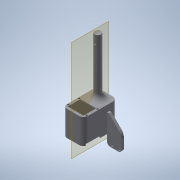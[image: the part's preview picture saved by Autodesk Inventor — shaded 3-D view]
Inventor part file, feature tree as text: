
AUTODESK INVENTOR PART (.ipt)
format: ipt  version: 2020.1 (Build 241239000, 239)  size: 274,432 bytes
history: native  units: mm
features: extrude x10, sketch x9, fillet x4, chamfer x1, plane x1, mirror x1
ambient origin geometry x8: Origin, YZ Plane, XZ Plane, XY Plane, X Axis, Y Axis, Z Axis, Center Point
bodies: Solid1 (feature_tree)
feature tree (26):
  sketch  "Sketch1"  dims[d0=25.0mm d1=45.5mm]
  extrude  "Extrusion1"  Depth=45.5mm
  extrude  "Extrusion2"  Depth=40.0mm TaperAngle=0.0deg
  extrude  "Extrusion3"  Depth=3.0mm
  extrude  "Extrusion4"  Depth=38.0mm TaperAngle=0.0deg
  fillet  "Fillet1"  Radius=10.3mm
  extrude  "Extrusion5"  Depth=90.0mm TaperAngle=0.0deg
  fillet  "Fillet2"  Radius=10.0mm
  extrude  "Extrusion6"  Depth=3.0mm
  extrude  "Extrusion7"  Depth=7.0mm
  chamfer  "Chamfer1"  Distance=3.0mm
  extrude  "Extrusion8"  Depth=3.0mm
  fillet  "Fillet3"  Radius=2.8mm
  extrude  "Extrusion9"  Depth=10.0mm
  fillet  "Fillet4"  Radius=2.8mm
  plane  "Work Plane1"
  mirror  "Mirror1"
  extrude  "Extrusion10"  Depth=10.0mm
  sketch  "Sketch2"  dims[d2=4.0mm d3=40.0mm d4=0.0mm]
  sketch  "Sketch3"  dims[d5=38.0mm d6=0.0mm d7=3.0mm]
  sketch  "Sketch4"  dims[d8=23.0mm d9=38.0mm d10=0.0mm d11=10.3mm]
  sketch  "Sketch5"  dims[d12=10.0mm d13=90.0mm d14=0.0mm d15=10.0mm]
  sketch  "Sketch6"  dims[d16=13.0mm d17=3.0mm]
  sketch  "Sketch7"  dims[d18=90.0mm d19=0.0mm d20=7.0mm]
  sketch  "Sketch8"  dims[d21=3.0mm]
  sketch  "Sketch9"  dims[d22=3.0mm d23=3.0mm d24=3.0mm d25=2.8mm d26=2.8mm d27=2.8mm d28=2.8mm d29=90.0mm d30=0.0mm d31=2.0mm d32=30.0mm d33=4.0mm d34=23.0mm d35=0.0mm d36=20.0mm d37=2.0mm d38=45.0deg d39=15.0mm d40=0.0mm d41=5.0mm d42=3.0mm d43=8.0mm d44=4.0mm d45=3.0mm d46=3.0mm d47=15.0mm d48=0.0mm d49=15.0mm d50=12.5mm d51=20.0mm d52=10.0mm d53=0.0mm]
